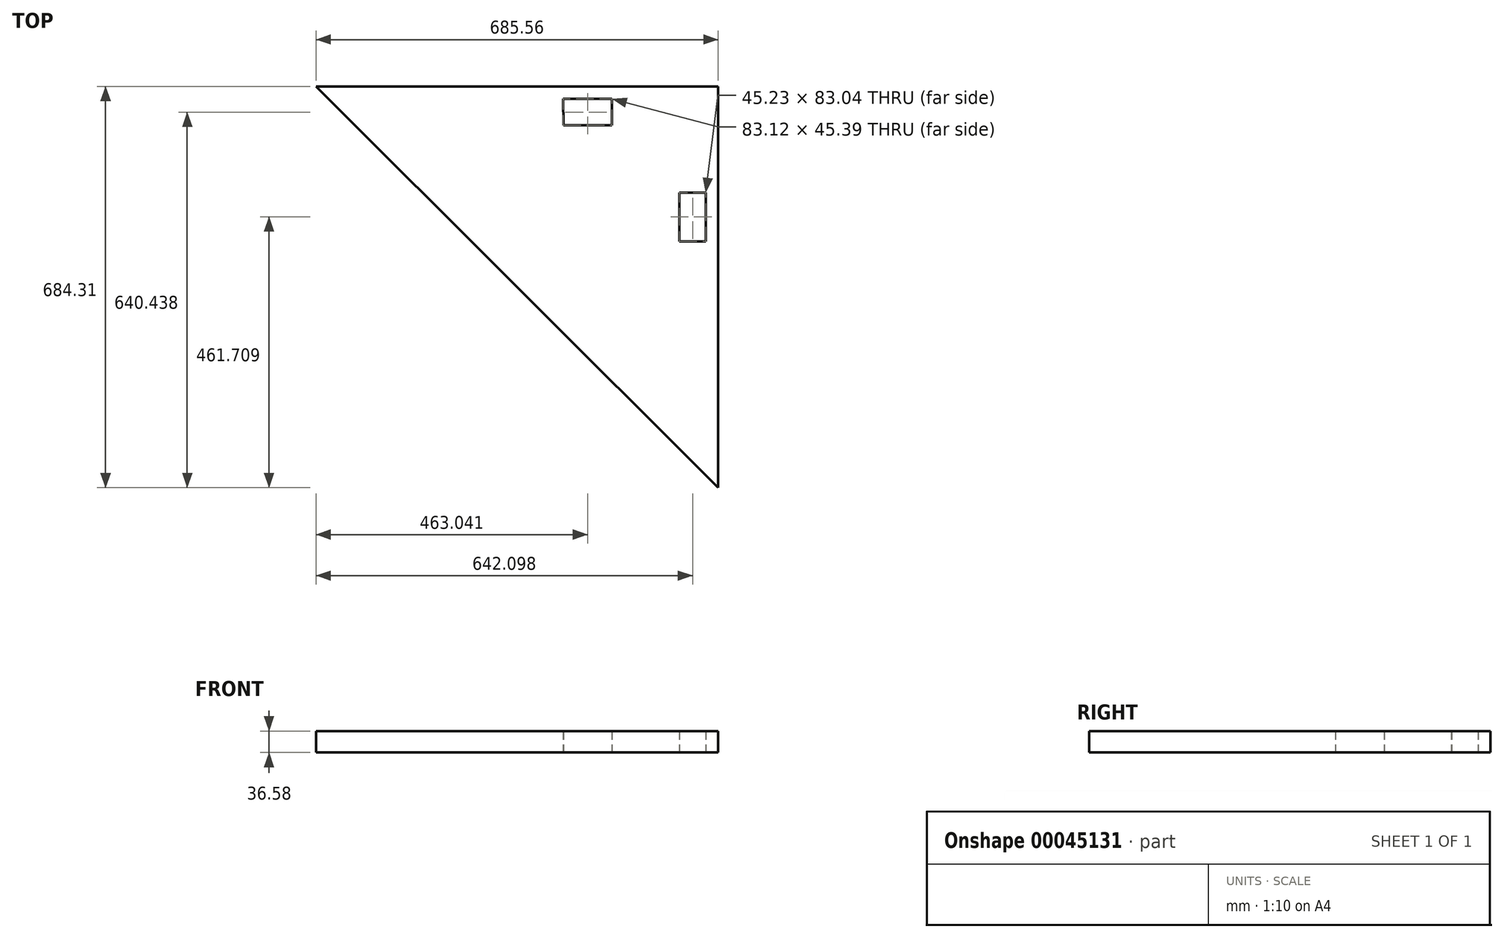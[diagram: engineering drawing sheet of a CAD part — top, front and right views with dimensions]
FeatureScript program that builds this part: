
annotation { "Feature Type Name" : "Feature", "Feature Type Description" : "" }
export const myFeature = defineFeature(function(context is Context, id is Id, definition is map)
    precondition{}
    {
        {
            var Q0;
            Q0=qCreatedBy(makeId("Top.planeOp"),FACE);
            var sketch = newSketch(context, id + "F0", { "sketchPlane" : qUnion([Q0])});
            skLineSegment(sketch, "E0", {"start": v(-452.87, 341.35) * mm, "end": v(232.7, -342.96) * mm});
            skLineSegment(sketch, "E1", {"start": v(232.7, -342.96) * mm, "end": v(232.7, 341.35) * mm});
            skLineSegment(sketch, "E2", {"start": v(232.7, 341.35) * mm, "end": v(-452.87, 341.35) * mm});
            skLineSegment(sketch, "E3", {"start": v(232.7, -0.8) * mm, "end": v(232.7, -342.96) * mm});
            skLineSegment(sketch, "E4", {"start": v(232.7, -171.88) * mm, "end": v(232.7, -342.96) * mm});
            skLineSegment(sketch, "E5.MirrorCS", {"start": v(51.65, 320.17) * mm, "end": v(-31.39, 320.02) * mm});
            skLineSegment(sketch, "E6.MirrorCS", {"start": v(51.65, 320.17) * mm, "end": v(51.73, 274.94) * mm});
            skLineSegment(sketch, "E7.MirrorCS", {"start": v(51.73, 274.94) * mm, "end": v(-31.3, 274.79) * mm});
            skLineSegment(sketch, "E8.MirrorCS", {"start": v(-31.39, 320.02) * mm, "end": v(-31.3, 274.79) * mm});
            skLineSegment(sketch, "E9.MirrorCS", {"start": v(166.61, 160.27) * mm, "end": v(166.61, 77.23) * mm});
            skLineSegment(sketch, "E10.MirrorCS", {"start": v(211.85, 77.23) * mm, "end": v(166.61, 77.23) * mm});
            skLineSegment(sketch, "E11.MirrorCS", {"start": v(211.85, 160.27) * mm, "end": v(211.85, 77.23) * mm});
            skLineSegment(sketch, "E12.MirrorCS", {"start": v(211.85, 160.27) * mm, "end": v(166.61, 160.27) * mm});
            skLineSegment(sketch, "E13", {"start": v(211.85, 77.23) * mm, "end": v(211.85, 160.27) * mm});
            skLineSegment(sketch, "E14", {"start": v(166.61, 77.23) * mm, "end": v(211.85, 77.23) * mm});
            skSolve(sketch);
        }
        {
            var Q0;
            Q0=makeQuery(id+"F0.imprint","IMPRINT",FACE,{"disambiguationData":[TD([[makeQuery(id+"F0.imprint","IMPRINT",EDGE,{"derivedFrom":sQuery(id+"F0.wireOp",EDGE,"E0")}),1.0]])]});
            extrude(context, id + "F1", {"entities" : qUnion([Q0]), "depth" : 36.58 * mm});
        }
        {
            var Q0;
            Q0=makeQuery(id+"F0.imprint","IMPRINT",FACE,{"disambiguationData":[TD([[makeQuery(id+"F0.imprint","IMPRINT",EDGE,{"derivedFrom":sQuery(id+"F0.wireOp",EDGE,"E1")}),1.0]])]});
            extrude(context, id + "F2", {"entities" : qUnion([Q0]), "operationType" : NewBodyOperationType.ADD, "depth" : 36.58 * mm});
        }
    });
